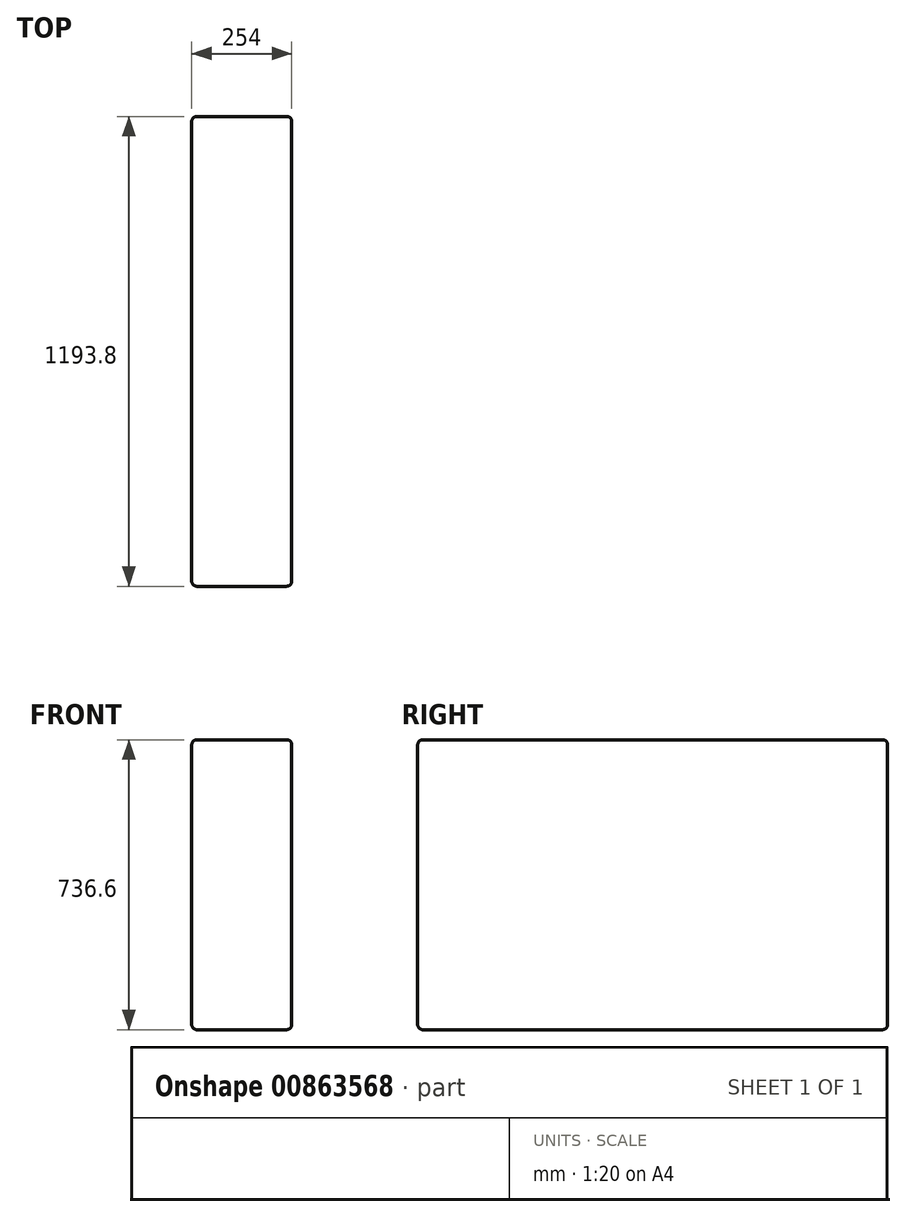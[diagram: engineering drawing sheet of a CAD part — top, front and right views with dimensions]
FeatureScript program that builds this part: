
annotation { "Feature Type Name" : "Feature", "Feature Type Description" : "" }
export const myFeature = defineFeature(function(context is Context, id is Id, definition is map)
    precondition{}
    {
        {
            var Q0;
            Q0=qCreatedBy(makeId("Top.planeOp"),FACE);
            var sketch = newSketch(context, id + "F0", { "sketchPlane" : qUnion([Q0])});
            skLineSegment(sketch, "E0.bottom", {"start": v(-430.82, 676.78) * mm, "end": v(-176.82, 676.78) * mm});
            skLineSegment(sketch, "E0.top", {"start": v(-430.82, -517.02) * mm, "end": v(-176.82, -517.02) * mm});
            skLineSegment(sketch, "E0.left", {"start": v(-430.82, 676.78) * mm, "end": v(-430.82, -517.02) * mm});
            skLineSegment(sketch, "E0.right", {"start": v(-176.82, 676.78) * mm, "end": v(-176.82, -517.02) * mm});
            skSolve(sketch);
        }
        {
            var Q0;
            Q0=makeQuery(id+"F0.imprint","IMPRINT",FACE,{"disambiguationData":[TD([[makeQuery(id+"F0.imprint","IMPRINT",EDGE,{"derivedFrom":sQuery(id+"F0.wireOp",EDGE,"E0.bottom")}),-1.0]])]});
            extrude(context, id + "F1", {"entities" : qUnion([Q0]), "depth" : 736.6 * mm, "offsetDistance" : 25.4 * mm});
        }
        {
            var Q0;
            Q0=makeQuery(id+"F1.opExtrude","CAP_EDGE",EDGE,{"disambiguationData":[OSD([sQuery(id+"F0.wireOp",EDGE,"E0.right")])],"isStart":true});
            var Q1;
            Q1=makeQuery(id+"F1.opExtrude","CAP_EDGE",EDGE,{"disambiguationData":[OSD([sQuery(id+"F0.wireOp",EDGE,"E0.right")])],"isStart":false});
            var Q2;
            Q2=makeQuery(id+"F1.opExtrude","CAP_EDGE",EDGE,{"disambiguationData":[OSD([sQuery(id+"F0.wireOp",EDGE,"E0.left")])],"isStart":false});
            var Q3;
            Q3=makeQuery(id+"F1.opExtrude","CAP_EDGE",EDGE,{"disambiguationData":[OSD([sQuery(id+"F0.wireOp",EDGE,"E0.top")])],"isStart":false});
            var Q4;
            Q4=makeQuery(id+"F1.opExtrude","CAP_EDGE",EDGE,{"disambiguationData":[OSD([sQuery(id+"F0.wireOp",EDGE,"E0.top")])],"isStart":true});
            var Q5;
            Q5=makeQuery(id+"F1.opExtrude","SWEPT_FACE",FACE,{"disambiguationData":[OSD([sQuery(id+"F0.wireOp",EDGE,"E0.right")])]});
            var Q6;
            Q6=makeQuery(id+"F1.opExtrude","SWEPT_FACE",FACE,{"disambiguationData":[OSD([sQuery(id+"F0.wireOp",EDGE,"E0.left")])]});
            var Q7;
            Q7=makeQuery(id+"F1.opExtrude","SWEPT_FACE",FACE,{"disambiguationData":[OSD([sQuery(id+"F0.wireOp",EDGE,"E0.top")])]});
            var Q8;
            Q8=makeQuery(id+"F1.opExtrude","SWEPT_EDGE",EDGE,{"disambiguationData":[OSD([sQuery(id+"F0.wireOp",EDGE,"E0.top"),sQuery(id+"F0.wireOp",EDGE,"E0.right")])]});
            var Q9;
            Q9=makeQuery(id+"F1.opExtrude","CAP_FACE",FACE,{"disambiguationData":[OSD([sQuery(id+"F0.wireOp",EDGE,"E0.bottom"),sQuery(id+"F0.wireOp",EDGE,"E0.top"),sQuery(id+"F0.wireOp",EDGE,"E0.left"),sQuery(id+"F0.wireOp",EDGE,"E0.right")])],"isStart":false});
            var Q10;
            Q10=makeQuery(id+"F1.opExtrude","SWEPT_EDGE",EDGE,{"disambiguationData":[OSD([sQuery(id+"F0.wireOp",EDGE,"E0.top"),sQuery(id+"F0.wireOp",EDGE,"E0.left")])]});
            var Q11;
            Q11=makeQuery(id+"F1.opExtrude","CAP_FACE",FACE,{"disambiguationData":[OSD([sQuery(id+"F0.wireOp",EDGE,"E0.bottom"),sQuery(id+"F0.wireOp",EDGE,"E0.top"),sQuery(id+"F0.wireOp",EDGE,"E0.left"),sQuery(id+"F0.wireOp",EDGE,"E0.right")])],"isStart":true});
            var Q12;
            Q12=makeQuery(id+"F1.opExtrude","SWEPT_EDGE",EDGE,{"disambiguationData":[OSD([sQuery(id+"F0.wireOp",EDGE,"E0.bottom"),sQuery(id+"F0.wireOp",EDGE,"E0.right")])]});
            var Q13;
            Q13=makeQuery(id+"F1.opExtrude","SWEPT_FACE",FACE,{"disambiguationData":[OSD([sQuery(id+"F0.wireOp",EDGE,"E0.bottom")])]});
            var Q14;
            Q14=makeQuery(id+"F1.opExtrude","CAP_EDGE",EDGE,{"disambiguationData":[OSD([sQuery(id+"F0.wireOp",EDGE,"E0.left")])],"isStart":true});
            var Q15;
            Q15=makeQuery(id+"F1.opExtrude","CAP_EDGE",EDGE,{"disambiguationData":[OSD([sQuery(id+"F0.wireOp",EDGE,"E0.bottom")])],"isStart":false});
            var Q16;
            Q16=makeQuery(id+"F1.opExtrude","CAP_EDGE",EDGE,{"disambiguationData":[OSD([sQuery(id+"F0.wireOp",EDGE,"E0.bottom")])],"isStart":true});
            var Q17;
            Q17=makeQuery(id+"F1.opExtrude","SWEPT_EDGE",EDGE,{"disambiguationData":[OSD([sQuery(id+"F0.wireOp",EDGE,"E0.bottom"),sQuery(id+"F0.wireOp",EDGE,"E0.left")])]});
            fillet(context, id + "F2", {"entities" : qUnion([Q0, Q1, Q2, Q3, Q4, Q5, Q6, Q7, Q8, Q9, Q10, Q11, Q12, Q13, Q14, Q15, Q16, Q17]), "radius" : 12.7 * mm, "tangentPropagation" : true, "allowEdgeOverflow" : false});
        }
    });
